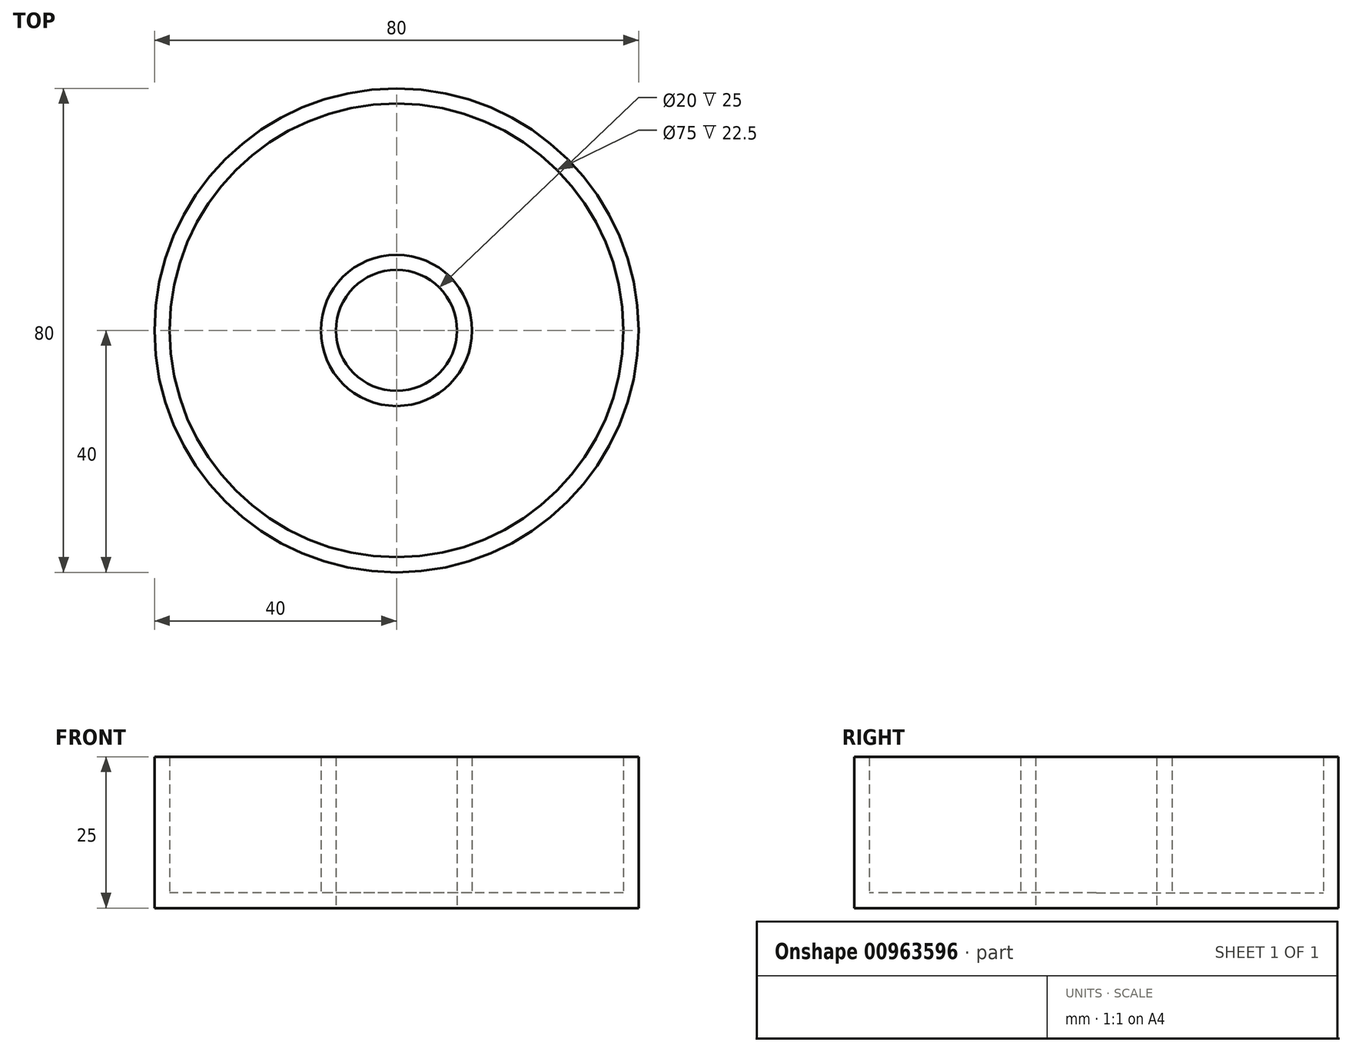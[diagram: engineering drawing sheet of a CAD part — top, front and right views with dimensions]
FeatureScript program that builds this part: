
annotation { "Feature Type Name" : "Feature", "Feature Type Description" : "" }
export const myFeature = defineFeature(function(context is Context, id is Id, definition is map)
    precondition{}
    {
        {
            var Q0;
            Q0=qCreatedBy(makeId("Front.planeOp"),FACE);
            var sketch = newSketch(context, id + "F0", { "sketchPlane" : qUnion([Q0])});
            skLineSegment(sketch, "E0", {"start": v(-70, 50) * mm, "end": v(-70, 0) * mm, "construction": true});
            skLineSegment(sketch, "E1", {"start": v(-70, 50) * mm, "end": v(0, 50) * mm, "construction": true});
            skLineSegment(sketch, "E2", {"start": v(0, 50) * mm, "end": v(70, 50) * mm, "construction": true});
            skLineSegment(sketch, "E3", {"start": v(70, 50) * mm, "end": v(70, 0) * mm, "construction": true});
            skLineSegment(sketch, "E4", {"start": v(70, 0) * mm, "end": v(70, -50) * mm, "construction": true});
            skLineSegment(sketch, "E5", {"start": v(70, -50) * mm, "end": v(0, -50) * mm, "construction": true});
            skLineSegment(sketch, "E6", {"start": v(0, -50) * mm, "end": v(-70, -50) * mm, "construction": true});
            skLineSegment(sketch, "E7", {"start": v(-70, -50) * mm, "end": v(-70, 0) * mm, "construction": true});
            skLineSegment(sketch, "E8", {"start": v(0, 0) * mm, "end": v(0, 50) * mm, "construction": true});
            skLineSegment(sketch, "E9", {"start": v(0, 0) * mm, "end": v(-70, 0) * mm, "construction": true});
            skLineSegment(sketch, "E10", {"start": v(-40, 12.5) * mm, "end": v(-40, -12.5) * mm});
            skLineSegment(sketch, "E11", {"start": v(-40, -12.5) * mm, "end": v(37.45, -12.5) * mm});
            skLineSegment(sketch, "E12", {"start": v(37.45, -12.5) * mm, "end": v(37.45, 12.5) * mm});
            skLineSegment(sketch, "E13", {"start": v(37.45, 12.5) * mm, "end": v(-40, 12.5) * mm});
            skLineSegment(sketch, "E14", {"start": v(0, 0) * mm, "end": v(-40, 0) * mm});
            skLineSegment(sketch, "E15", {"start": v(-10, 12.5) * mm, "end": v(-10, -12.5) * mm});
            skLineSegment(sketch, "E16.MirrorCS", {"start": v(10, 12.5) * mm, "end": v(10, -12.5) * mm});
            skSolve(sketch);
        }
        {
            var Q0;
            {var subQ0=sQuery(id+"F0.wireOp",EDGE,"E13");var subQ1=sQuery(id+"F0.wireOp",EDGE,"E10");var subQ2=makeQuery(id+"F0.imprint","INTERSECT",VERTEX,{"derivedFrom":[subQ1,subQ0]});Q0=makeQuery(id+"F0.imprint","IMPRINT",FACE,{"disambiguationData":[TD([[makeQuery(id+"F0.imprint","IMPRINT",EDGE,{"disambiguationData":[TD([[subQ2,-1.0]])],"derivedFrom":subQ1}),1.0]])]});}
            var Q1;
            {var subQ0=sQuery(id+"F0.wireOp",EDGE,"E11");var subQ1=sQuery(id+"F0.wireOp",EDGE,"E10");var subQ2=makeQuery(id+"F0.imprint","INTERSECT",VERTEX,{"derivedFrom":[subQ1,subQ0]});Q1=makeQuery(id+"F0.imprint","IMPRINT",FACE,{"disambiguationData":[TD([[makeQuery(id+"F0.imprint","IMPRINT",EDGE,{"disambiguationData":[TD([[subQ2,1.0]])],"derivedFrom":subQ1}),1.0]])]});}
            var Q2;
            Q2=sQuery(id+"F0.wireOp",EDGE,"E8");
            revolve(context, id + "F1", {"surfaceOperationType" : NewSurfaceOperationType.NEW, "entities" : qUnion([Q0, Q1]), "axis" : qUnion([Q2]), "revolveType" : RevolveType.FULL});
        }
        {
            var Q0;
            Q0=makeQuery(id+"F1.opRevolve","SWEPT_FACE",FACE,{"disambiguationData":[OSD([sQuery(id+"F0.wireOp",EDGE,"E13")])]});
            shell(context, id + "F2", {"entities" : qUnion([Q0]), "thickness" : 2.5 * mm});
        }
    });
